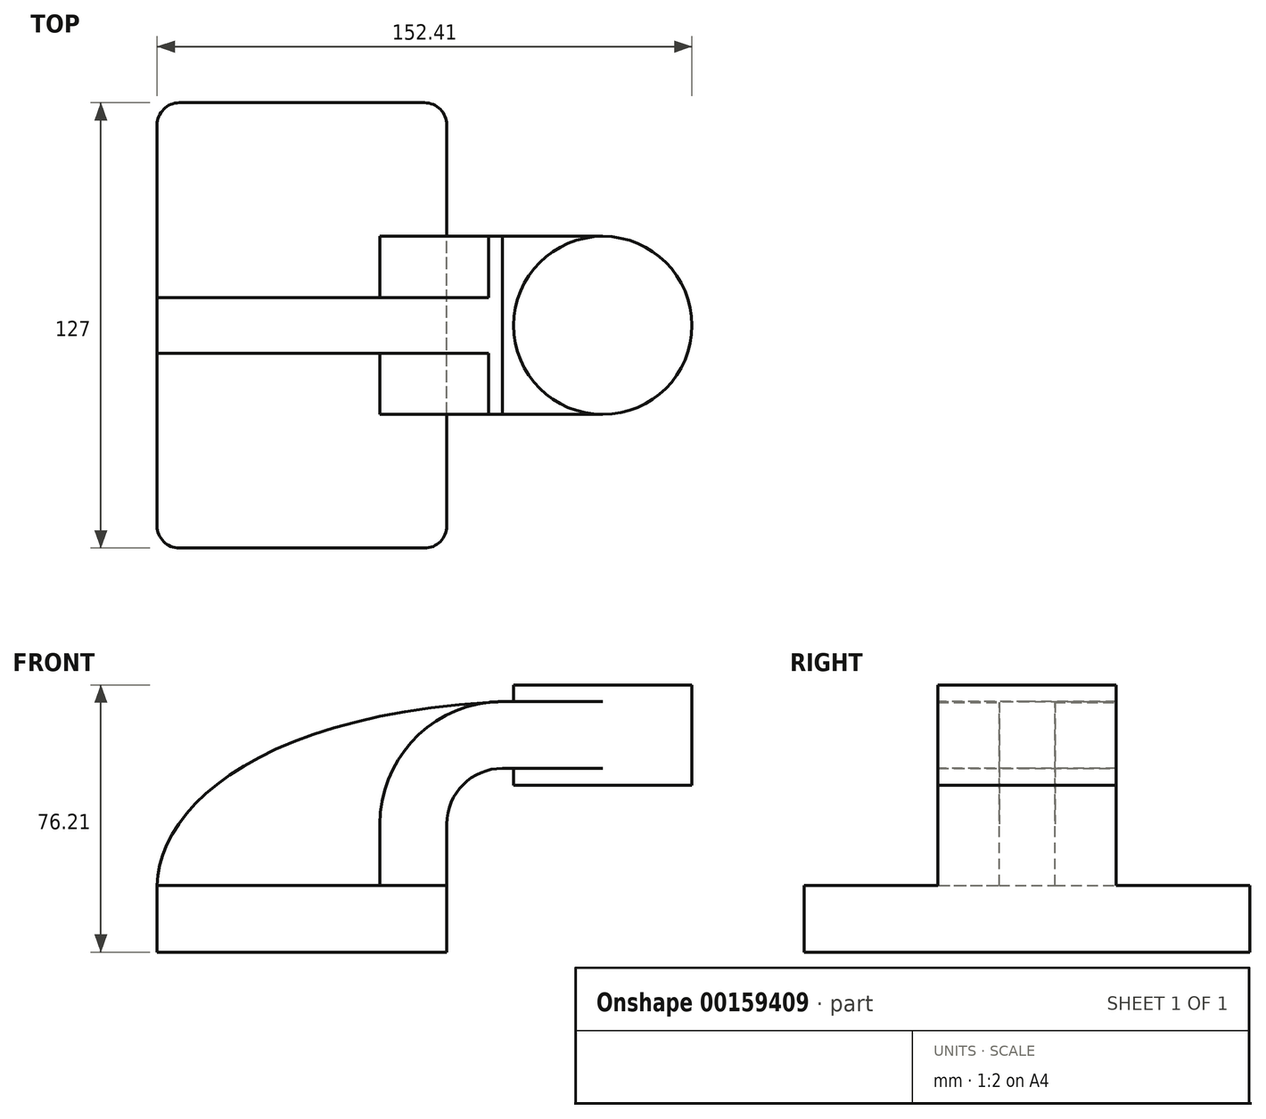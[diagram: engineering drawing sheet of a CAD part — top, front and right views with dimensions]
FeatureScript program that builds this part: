
annotation { "Feature Type Name" : "Feature", "Feature Type Description" : "" }
export const myFeature = defineFeature(function(context is Context, id is Id, definition is map)
    precondition{}
    {
        {
            var Q0;
            Q0=qCreatedBy(makeId("Front.planeOp"),FACE);
            var sketch = newSketch(context, id + "F0", { "sketchPlane" : qUnion([Q0])});
            skLineSegment(sketch, "E0.bottom", {"start": v(-41.28, 9.52) * mm, "end": v(41.27, 9.53) * mm});
            skLineSegment(sketch, "E0.top", {"start": v(-41.28, -9.52) * mm, "end": v(41.28, -9.52) * mm});
            skLineSegment(sketch, "E0.left", {"start": v(-41.28, 9.52) * mm, "end": v(-41.28, -9.52) * mm});
            skLineSegment(sketch, "E0.right", {"start": v(41.27, 9.53) * mm, "end": v(41.28, -9.52) * mm});
            skPoint(sketch, "E0.middle", {"position": v(0, 0) * mm});
            skLineSegment(sketch, "E1.bottom", {"start": v(111.12, 38.1) * mm, "end": v(60.32, 38.1) * mm});
            skLineSegment(sketch, "E1.top", {"start": v(111.12, 66.68) * mm, "end": v(60.32, 66.68) * mm});
            skLineSegment(sketch, "E1.left", {"start": v(111.12, 38.1) * mm, "end": v(111.12, 66.68) * mm});
            skLineSegment(sketch, "E1.right", {"start": v(60.32, 38.1) * mm, "end": v(60.32, 66.68) * mm});
            skPoint(sketch, "E1.middle", {"position": v(85.72, 52.39) * mm});
            skLineSegment(sketch, "E2", {"start": v(41.27, 9.53) * mm, "end": v(41.27, 27) * mm});
            skArc(sketch, "E3", {"start": v(41.27, 27) * mm, "mid": v(45.92, 38.23) * mm, "end": v(57.15, 42.88) * mm});
            skLineSegment(sketch, "E4", {"start": v(57.15, 42.88) * mm, "end": v(85.72, 42.88) * mm});
            skLineSegment(sketch, "E5.0", {"start": v(57.15, 61.93) * mm, "end": v(85.72, 61.93) * mm});
            skArc(sketch, "E5.1", {"start": v(22.22, 27) * mm, "mid": v(32.45, 51.7) * mm, "end": v(57.15, 61.93) * mm});
            skLineSegment(sketch, "E5.2", {"start": v(22.22, 9.53) * mm, "end": v(22.22, 27) * mm});
            skLineSegment(sketch, "E6", {"start": v(85.72, 38.1) * mm, "end": v(85.72, 66.68) * mm});
            skFitSpline(sketch, "E7", {"points": [v(-41.28, 9.52) * mm, v(57.15, 61.93) * mm], "startDerivative": vector(1.23, 66.93) * mm, "endDerivative": vector(206.66, 10.16) * mm});
            skSolve(sketch);
        }
        {
            var Q0;
            Q0=makeQuery(id+"F0.imprint","IMPRINT",FACE,{"disambiguationData":[TD([[makeQuery(id+"F0.imprint","IMPRINT",EDGE,{"derivedFrom":sQuery(id+"F0.wireOp",EDGE,"E0.top")}),1.0]])]});
            extrude(context, id + "F1", {"entities" : qUnion([Q0]), "endBound" : BoundingType.SYMMETRIC, "depth" : 127 * mm});
        }
        {
            var Q0;
            {var subQ0=sQuery(id+"F0.wireOp",EDGE,"E4");var subQ1=sQuery(id+"F0.wireOp",EDGE,"E1.right");var subQ2=makeQuery(id+"F0.imprint","INTERSECT",VERTEX,{"derivedFrom":[subQ1,subQ0]});Q0=makeQuery(id+"F0.imprint","IMPRINT",FACE,{"disambiguationData":[TD([[makeQuery(id+"F0.imprint","IMPRINT",EDGE,{"disambiguationData":[TD([[subQ2,-1.0]])],"derivedFrom":subQ1}),-1.0]])]});}
            var Q1;
            {var subQ1=sQuery(id+"F0.wireOp",EDGE,"E2");Q1=makeQuery(id+"F0.imprint","IMPRINT",FACE,{"disambiguationData":[TD([[makeQuery(id+"F0.imprint","IMPRINT",EDGE,{"derivedFrom":subQ1}),1.0]])]});}
            extrude(context, id + "F2", {"entities" : qUnion([Q0, Q1]), "operationType" : NewBodyOperationType.ADD, "endBound" : BoundingType.SYMMETRIC, "depth" : 50.8 * mm});
        }
        {
            var Q0;
            {var subQ3=sQuery(id+"F0.wireOp",EDGE,"E5.2");Q0=makeQuery(id+"F0.imprint","IMPRINT",FACE,{"disambiguationData":[TD([[makeQuery(id+"F0.imprint","IMPRINT",EDGE,{"derivedFrom":subQ3}),1.0]])]});}
            extrude(context, id + "F3", {"entities" : qUnion([Q0]), "operationType" : NewBodyOperationType.ADD, "endBound" : BoundingType.SYMMETRIC, "depth" : 15.88 * mm});
        }
        {
            var Q0;
            {var subQ0=sQuery(id+"F0.wireOp",EDGE,"E1.left");Q0=makeQuery(id+"F0.imprint","IMPRINT",FACE,{"disambiguationData":[TD([[makeQuery(id+"F0.imprint","IMPRINT",EDGE,{"derivedFrom":subQ0}),1.0]])]});}
            var Q1;
            Q1=sQuery(id+"F0.wireOp",EDGE,"E6");
            revolve(context, id + "F4", {"operationType" : NewBodyOperationType.ADD, "entities" : qUnion([Q0]), "axis" : qUnion([Q1]), "revolveType" : RevolveType.FULL});
        }
        {
            var Q0;
            Q0=makeQuery(id+"F1.opExtrude","CAP_EDGE",EDGE,{"disambiguationData":[OSD([sQuery(id+"F0.wireOp",EDGE,"E0.right")])],"isStart":false});
            var Q1;
            Q1=makeQuery(id+"F1.opExtrude","CAP_EDGE",EDGE,{"disambiguationData":[OSD([sQuery(id+"F0.wireOp",EDGE,"E0.left")])],"isStart":false});
            var Q2;
            Q2=makeQuery(id+"F1.opExtrude","CAP_EDGE",EDGE,{"disambiguationData":[OSD([sQuery(id+"F0.wireOp",EDGE,"E0.right")])],"isStart":true});
            var Q3;
            Q3=makeQuery(id+"F1.opExtrude","CAP_EDGE",EDGE,{"disambiguationData":[OSD([sQuery(id+"F0.wireOp",EDGE,"E0.left")])],"isStart":true});
            fillet(context, id + "F5", {"entities" : qUnion([Q0, Q1, Q2, Q3]), "radius" : 6.35 * mm, "tangentPropagation" : true, "allowEdgeOverflow" : false});
        }
    });
